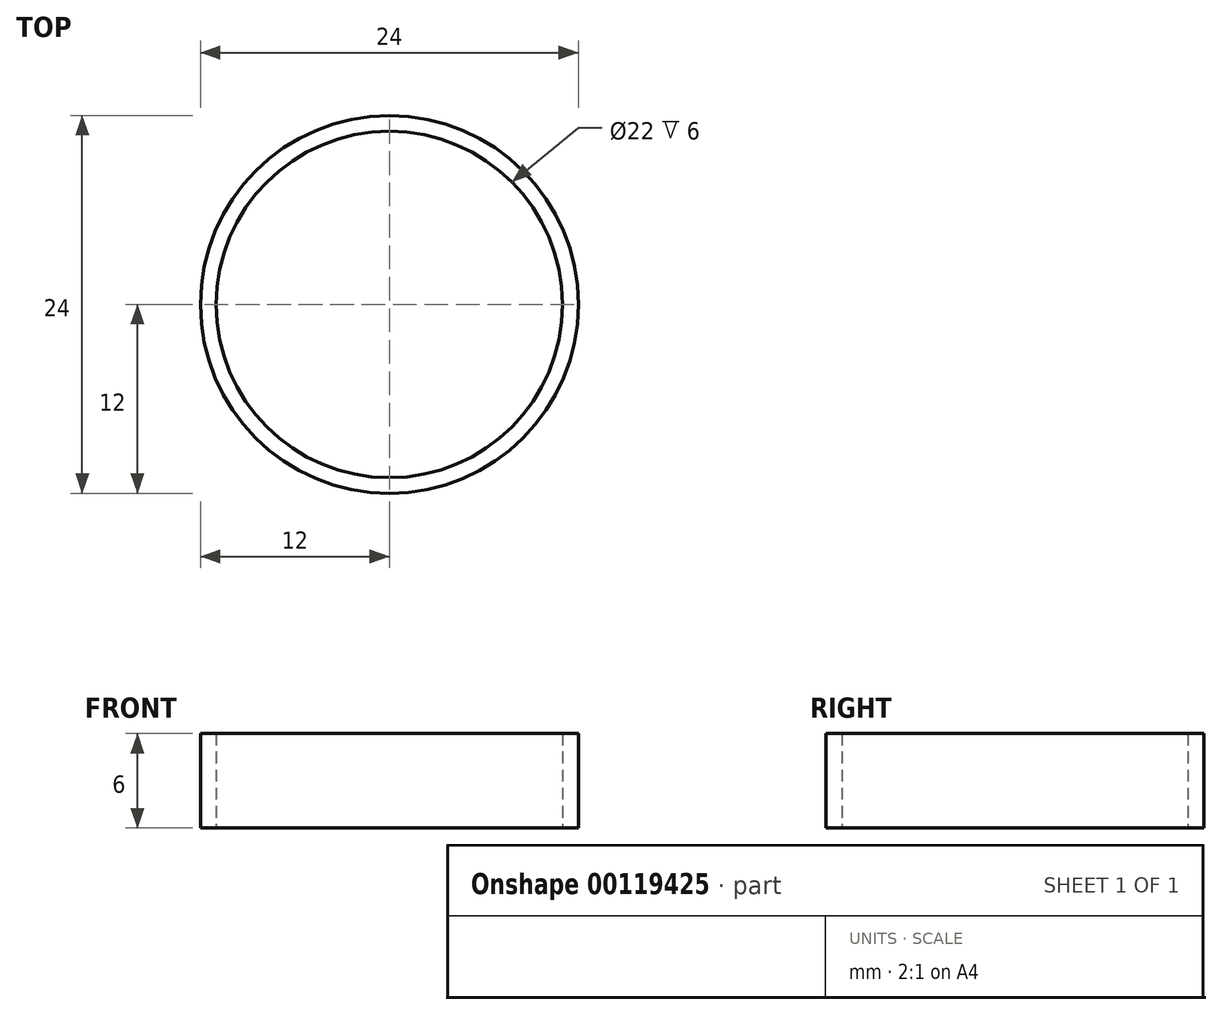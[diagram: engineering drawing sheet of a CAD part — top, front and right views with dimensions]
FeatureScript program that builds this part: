
annotation { "Feature Type Name" : "Feature", "Feature Type Description" : "" }
export const myFeature = defineFeature(function(context is Context, id is Id, definition is map)
    precondition{}
    {
        {
            assignVariable(context, id + "F0", {"name" : "h", "anyValue" : 6 * mm});
        }
        {
            var Q0;
            Q0=qCreatedBy(makeId("Top.planeOp"),FACE);
            var sketch = newSketch(context, id + "F1", { "sketchPlane" : qUnion([Q0])});
            skCircle(sketch, "E0", {"center": v(0, 0) * mm, "radius": 11 * mm});
            skCircle(sketch, "E1.0", {"center": v(0, 0) * mm, "radius": 12 * mm});
            skSolve(sketch);
        }
        {
            var Q0;
            Q0=makeQuery(id+"F1.imprint","IMPRINT",FACE,{"disambiguationData":[TD([[makeQuery(id+"F1.imprint","IMPRINT",EDGE,{"derivedFrom":sQuery(id+"F1.wireOp",EDGE,"E0")}),-1.0]])]});
            extrude(context, id + "F2", {"entities" : qUnion([Q0]), "depth" : getVariable(context, 'h')});
        }
    });
